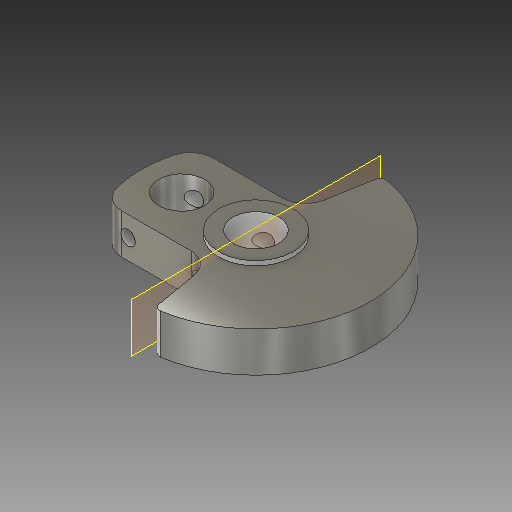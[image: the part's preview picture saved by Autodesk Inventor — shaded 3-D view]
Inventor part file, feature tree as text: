
AUTODESK INVENTOR PART (.ipt)
format: ipt  version: 2017 (Build 210142000, 142)  size: 225,792 bytes
history: native  units: mm
features: extrude x4, fillet x4, sketch x2, plane x2, projected_geometry x2
ambient origin geometry x8: Origin, YZ Plane, XZ Plane, XY Plane, X Axis, Y Axis, Z Axis, Center Point
bodies: Body1 (feature_tree)
feature tree (14):
  sketch  "Sketch1"  dims[d0=40.0mm d1=8.0mm]
  extrude  "Extrusion4"  Depth=8.0mm
  extrude  "Extrusion5"  Depth=10.0mm
  fillet  "Fillet1"  Radius=20.0mm
  fillet  "Fillet2"  Radius=17.453293mm
  fillet  "Fillet3"  Radius=17.453293mm
  fillet  "Fillet4"  Radius=40.0mm
  plane  "Work Plane1"
  extrude  "Extrusion6"  Depth=10.0mm
  plane  "Work Plane2"
  extrude  "Extrusion7"  Depth=10.0mm
  sketch  "Sketch3"  dims[d2=16.0mm d3=20.0mm d4=20.0mm d5=17.453293mm d6=17.453293mm d7=40.0mm d8=20.0mm d10=8.0mm d14=8.0mm d15=13.0mm d16=13.0mm d21=7.0mm d24=7.0mm d25=0.0mm d26=7.8mm d27=0.0mm d28=4.0mm d29=4.0mm d30=4.0mm d31=1.0mm d32=0.0mm d33=2.5mm d34=11.0mm d35=3.497732mm d37=10.0mm d38=0.0mm d39=11.5mm d43=10.0mm d44=0.0mm d45=5.0mm d46=7.0mm d47=5.0mm d48=3.5mm d50=2.5mm]
  projected_geometry  "Projected Loop1"
  projected_geometry  "Projected Loop2"
